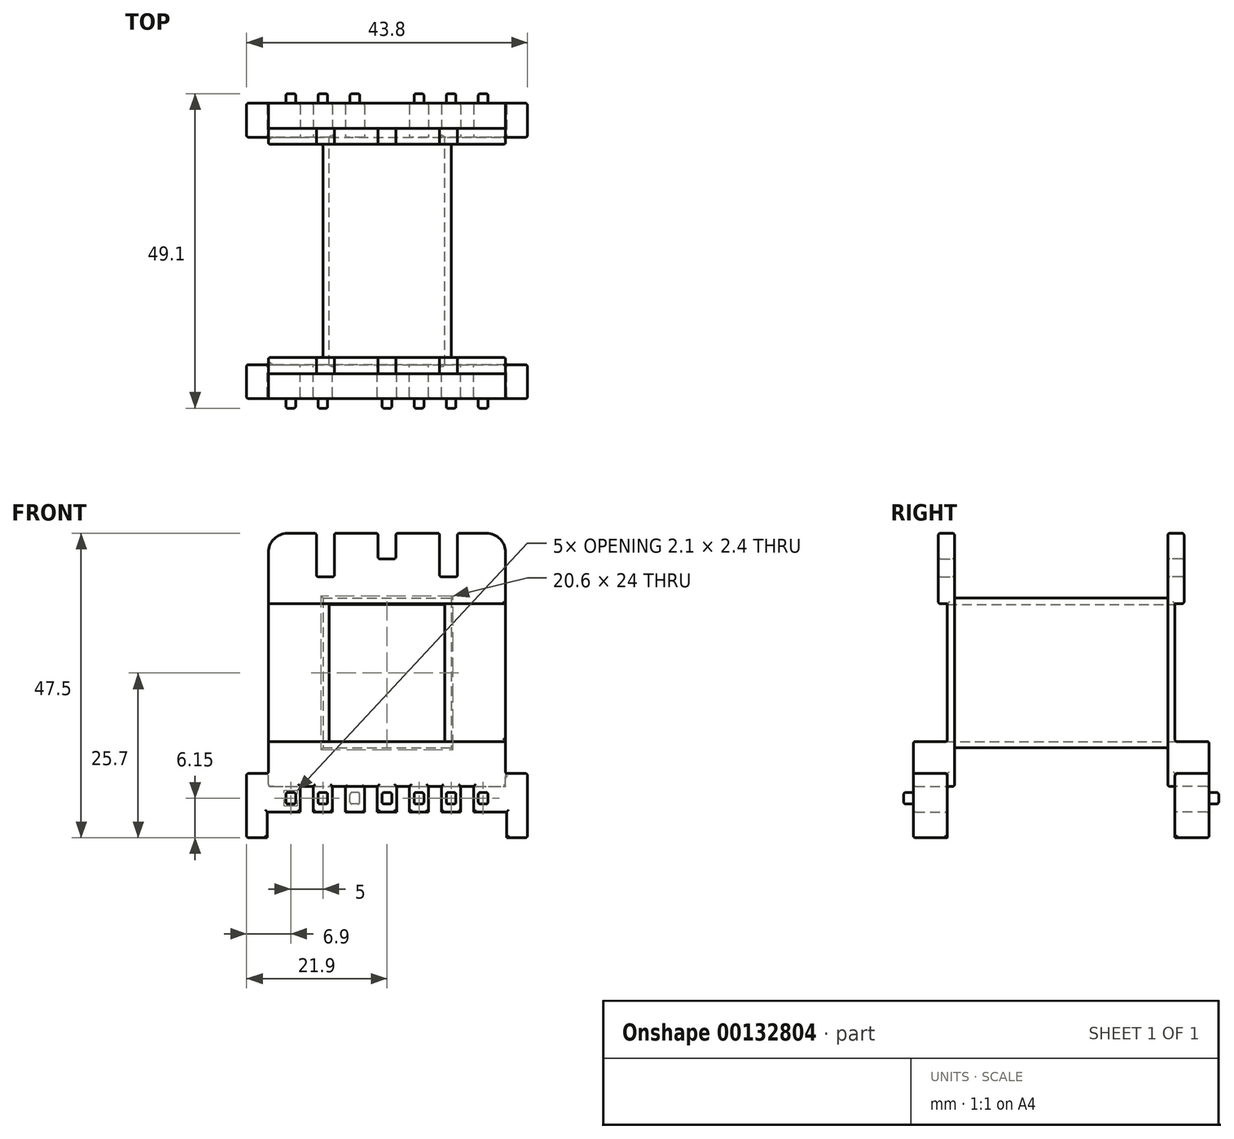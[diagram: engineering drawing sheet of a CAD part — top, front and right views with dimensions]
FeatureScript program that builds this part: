
annotation { "Feature Type Name" : "Feature", "Feature Type Description" : "" }
export const myFeature = defineFeature(function(context is Context, id is Id, definition is map)
    precondition{}
    {
        {
            var Q0;
            Q0=qCreatedBy(makeId("Front.planeOp"),FACE);
            var sketch = newSketch(context, id + "F0", { "sketchPlane" : qUnion([Q0])});
            skLineSegment(sketch, "E0.bottom", {"start": v(-18.5, 8) * mm, "end": v(18.5, 8) * mm});
            skLineSegment(sketch, "E0.left", {"start": v(-18.5, 8) * mm, "end": v(-18.5, 47.5) * mm});
            skLineSegment(sketch, "E0.right", {"start": v(18.5, 8) * mm, "end": v(18.5, 47.5) * mm});
            skLineSegment(sketch, "E1", {"start": v(-18.5, 47.5) * mm, "end": v(-11, 47.5) * mm});
            skLineSegment(sketch, "E2", {"start": v(-11, 47.5) * mm, "end": v(-11, 40.7) * mm});
            skLineSegment(sketch, "E3", {"start": v(-11, 40.7) * mm, "end": v(-8.2, 40.7) * mm});
            skLineSegment(sketch, "E4", {"start": v(-8.2, 40.7) * mm, "end": v(-8.2, 47.5) * mm});
            skLineSegment(sketch, "E5", {"start": v(-8.2, 47.5) * mm, "end": v(-1.4, 47.5) * mm});
            skLineSegment(sketch, "E6", {"start": v(-1.4, 47.5) * mm, "end": v(-1.4, 43.5) * mm});
            skLineSegment(sketch, "E7", {"start": v(-1.4, 43.5) * mm, "end": v(1.4, 43.5) * mm});
            skLineSegment(sketch, "E8", {"start": v(1.4, 43.5) * mm, "end": v(1.4, 47.5) * mm});
            skLineSegment(sketch, "E9", {"start": v(1.4, 47.5) * mm, "end": v(8.2, 47.5) * mm});
            skLineSegment(sketch, "E10", {"start": v(8.2, 47.5) * mm, "end": v(8.2, 40.7) * mm});
            skLineSegment(sketch, "E11", {"start": v(8.2, 40.7) * mm, "end": v(11, 40.7) * mm});
            skLineSegment(sketch, "E12", {"start": v(11, 40.7) * mm, "end": v(11, 47.5) * mm});
            skLineSegment(sketch, "E13", {"start": v(11, 47.5) * mm, "end": v(18.5, 47.5) * mm});
            skSolve(sketch);
        }
        {
            var Q0;
            Q0=makeQuery(id+"F0.imprint","IMPRINT",FACE,{"disambiguationData":[TD([[makeQuery(id+"F0.imprint","IMPRINT",EDGE,{"derivedFrom":sQuery(id+"F0.wireOp",EDGE,"E0.bottom")}),1.0]])]});
            var sketch = newSketch(context, id + "F1", { "sketchPlane" : qUnion([Q0])});
            skLineSegment(sketch, "E14.bottom", {"start": v(-9, 15) * mm, "end": v(9, 15) * mm});
            skLineSegment(sketch, "E14.top", {"start": v(-9, 36.4) * mm, "end": v(9, 36.4) * mm});
            skLineSegment(sketch, "E14.left", {"start": v(-9, 15) * mm, "end": v(-9, 36.4) * mm});
            skLineSegment(sketch, "E14.right", {"start": v(9, 15) * mm, "end": v(9, 36.4) * mm});
            skSolve(sketch);
        }
        {
            var Q0;
            Q0=makeQuery(id+"F1.imprint","IMPRINT",FACE,{"disambiguationData":[TD([[makeQuery(id+"F1.imprint","IMPRINT",EDGE,{"derivedFrom":sQuery(id+"F1.wireOp",EDGE,"E14.bottom")}),-1.0]])]});
            extrude(context, id + "F2", {"entities" : qUnion([Q0]), "depth" : 17.75 * mm, "hasSecondDirection" : true, "secondDirectionOppositeDirection" : false, "secondDirectionDepth" : 16.65 * mm});
        }
        {
            var Q0;
            Q0=makeQuery(id+"F2.opExtrude","SWEPT_BODY",BODY,{"disambiguationData":[OSD([sQuery(id+"F0.wireOp",EDGE,"E0.bottom"),sQuery(id+"F0.wireOp",EDGE,"E0.top"),sQuery(id+"F0.wireOp",EDGE,"E0.left"),sQuery(id+"F0.wireOp",EDGE,"E0.right"),sQuery(id+"F1.wireOp",EDGE,"E14.bottom"),sQuery(id+"F1.wireOp",EDGE,"E14.top"),sQuery(id+"F1.wireOp",EDGE,"E14.left"),sQuery(id+"F1.wireOp",EDGE,"E14.right")])]});
            var Q1;
            Q1=makeQuery(id+"F0.imprint","IMPRINT",FACE,{"disambiguationData":[TD([[makeQuery(id+"F0.imprint","IMPRINT",EDGE,{"derivedFrom":sQuery(id+"F0.wireOp",EDGE,"E0.bottom")}),1.0]])]});
            mirror(context, id + "F3", {"operationType" : NewBodyOperationType.ADD, "entities" : qUnion([Q0]), "mirrorPlane" : qUnion([Q1])});
        }
        {
            var Q0;
            Q0=makeQuery(id+"F0.imprint","IMPRINT",FACE,{"disambiguationData":[TD([[makeQuery(id+"F0.imprint","IMPRINT",EDGE,{"derivedFrom":sQuery(id+"F0.wireOp",EDGE,"E0.bottom")}),1.0]])]});
            var sketch = newSketch(context, id + "F4", { "sketchPlane" : qUnion([Q0])});
            skLineSegment(sketch, "E15.bottom", {"start": v(-10, 37.4) * mm, "end": v(10, 37.4) * mm});
            skLineSegment(sketch, "E15.top", {"start": v(-10, 14) * mm, "end": v(10, 14) * mm});
            skLineSegment(sketch, "E15.left", {"start": v(-10, 37.4) * mm, "end": v(-10, 14) * mm});
            skLineSegment(sketch, "E15.right", {"start": v(10, 37.4) * mm, "end": v(10, 14) * mm});
            skSolve(sketch);
        }
        {
            var Q0;
            Q0=makeQuery(id+"F4.imprint","IMPRINT",FACE,{"disambiguationData":[TD([[makeQuery(id+"F4.imprint","IMPRINT",EDGE,{"derivedFrom":sQuery(id+"F4.wireOp",EDGE,"E15.bottom")}),-1.0]])]});
            var sketch = newSketch(context, id + "F5", { "sketchPlane" : qUnion([Q0])});
            skLineSegment(sketch, "E16.bottom", {"start": v(-9, 36.4) * mm, "end": v(9, 36.4) * mm});
            skLineSegment(sketch, "E16.top", {"start": v(-9, 15) * mm, "end": v(9, 15) * mm});
            skLineSegment(sketch, "E16.left", {"start": v(-9, 36.4) * mm, "end": v(-9, 15) * mm});
            skLineSegment(sketch, "E16.right", {"start": v(9, 36.4) * mm, "end": v(9, 15) * mm});
            skSolve(sketch);
        }
        {
            var Q0;
            Q0=makeQuery(id+"F5.imprint","IMPRINT",FACE,{"disambiguationData":[TD([[makeQuery(id+"F5.imprint","IMPRINT",EDGE,{"derivedFrom":sQuery(id+"F5.wireOp",EDGE,"E16.bottom")}),1.0]])]});
            extrude(context, id + "F6", {"entities" : qUnion([Q0]), "operationType" : NewBodyOperationType.ADD, "endBound" : BoundingType.SYMMETRIC, "depth" : 35 * mm});
        }
        {
            var Q0;
            Q0=makeQuery(id+"F2.opExtrude","CAP_FACE",FACE,{"disambiguationData":[OSD([sQuery(id+"F0.wireOp",EDGE,"E0.bottom"),sQuery(id+"F0.wireOp",EDGE,"E0.top"),sQuery(id+"F0.wireOp",EDGE,"E0.left"),sQuery(id+"F0.wireOp",EDGE,"E0.right"),sQuery(id+"F1.wireOp",EDGE,"E14.bottom"),sQuery(id+"F1.wireOp",EDGE,"E14.top"),sQuery(id+"F1.wireOp",EDGE,"E14.left"),sQuery(id+"F1.wireOp",EDGE,"E14.right")])],"isStart":false});
            var sketch = newSketch(context, id + "F7", { "sketchPlane" : qUnion([Q0])});
            skLineSegment(sketch, "E17", {"start": v(-21.9, 0) * mm, "end": v(-21.9, 10) * mm});
            skLineSegment(sketch, "E18", {"start": v(-21.9, 10) * mm, "end": v(-18.5, 10) * mm});
            skLineSegment(sketch, "E19", {"start": v(-18.5, 10) * mm, "end": v(-18.5, 15) * mm});
            skLineSegment(sketch, "E20", {"start": v(-18.5, 15) * mm, "end": v(18.5, 15) * mm});
            skLineSegment(sketch, "E21", {"start": v(18.5, 15) * mm, "end": v(18.5, 10) * mm});
            skLineSegment(sketch, "E22", {"start": v(18.5, 10) * mm, "end": v(21.9, 10) * mm});
            skLineSegment(sketch, "E23", {"start": v(21.9, 10) * mm, "end": v(21.9, 0) * mm});
            skLineSegment(sketch, "E24", {"start": v(21.9, 0) * mm, "end": v(18.65, 0) * mm});
            skLineSegment(sketch, "E25", {"start": v(18.65, 0) * mm, "end": v(18.65, 4) * mm});
            skLineSegment(sketch, "E26", {"start": v(-18.65, 4) * mm, "end": v(-18.65, 0) * mm});
            skLineSegment(sketch, "E27", {"start": v(-18.65, 0) * mm, "end": v(-21.9, 0) * mm});
            skLineSegment(sketch, "E28", {"start": v(-18.65, 4) * mm, "end": v(-13.5, 4) * mm});
            skLineSegment(sketch, "E29", {"start": v(-13.5, 4) * mm, "end": v(-13.5, 8) * mm});
            skLineSegment(sketch, "E30", {"start": v(-13.5, 8) * mm, "end": v(-11.5, 8) * mm});
            skLineSegment(sketch, "E31", {"start": v(-11.5, 8) * mm, "end": v(-11.5, 4) * mm});
            skLineSegment(sketch, "E32", {"start": v(-11.5, 4) * mm, "end": v(-8.5, 4) * mm});
            skLineSegment(sketch, "E33", {"start": v(-8.5, 4) * mm, "end": v(-8.5, 8) * mm});
            skLineSegment(sketch, "E34", {"start": v(-8.5, 8) * mm, "end": v(-1.5, 8) * mm});
            skLineSegment(sketch, "E35", {"start": v(-1.5, 8) * mm, "end": v(-1.5, 4) * mm});
            skLineSegment(sketch, "E36", {"start": v(-1.5, 4) * mm, "end": v(0, 4) * mm});
            skLineSegment(sketch, "E37.MirrorCS", {"start": v(13.5, 8) * mm, "end": v(11.5, 8) * mm});
            skLineSegment(sketch, "E38.MirrorCS", {"start": v(6.5, 4) * mm, "end": v(3.5, 4) * mm});
            skLineSegment(sketch, "E39.MirrorCS", {"start": v(8.5, 8) * mm, "end": v(6.5, 8) * mm});
            skLineSegment(sketch, "E40.MirrorCS", {"start": v(11.5, 8) * mm, "end": v(11.5, 4) * mm});
            skLineSegment(sketch, "E41.MirrorCS", {"start": v(6.5, 8) * mm, "end": v(6.5, 4) * mm});
            skLineSegment(sketch, "E42.MirrorCS", {"start": v(1.5, 8) * mm, "end": v(1.5, 4) * mm});
            skLineSegment(sketch, "E43.MirrorCS", {"start": v(1.5, 4) * mm, "end": v(0, 4) * mm});
            skLineSegment(sketch, "E44.MirrorCS", {"start": v(13.5, 4) * mm, "end": v(13.5, 8) * mm});
            skLineSegment(sketch, "E45.MirrorCS", {"start": v(3.5, 4) * mm, "end": v(3.5, 8) * mm});
            skLineSegment(sketch, "E46.MirrorCS", {"start": v(11.5, 4) * mm, "end": v(8.5, 4) * mm});
            skLineSegment(sketch, "E47.MirrorCS", {"start": v(18.65, 4) * mm, "end": v(13.5, 4) * mm});
            skLineSegment(sketch, "E48.MirrorCS", {"start": v(18.65, 4) * mm, "end": v(18.65, 0) * mm});
            skLineSegment(sketch, "E49.MirrorCS", {"start": v(3.5, 8) * mm, "end": v(1.5, 8) * mm});
            skLineSegment(sketch, "E50.MirrorCS", {"start": v(8.5, 4) * mm, "end": v(8.5, 8) * mm});
            skSolve(sketch);
        }
        {
            var Q0;
            {var subQ8=sQuery(id+"F7.wireOp",EDGE,"E19");Q0=makeQuery(id+"F7.imprint","IMPRINT",FACE,{"disambiguationData":[TD([[makeQuery(id+"F7.imprint","IMPRINT",EDGE,{"derivedFrom":subQ8}),-1.0]])]});}
            var Q1;
            Q1=makeQuery(id+"F7.imprint","IMPRINT",FACE,{"disambiguationData":[TD([[makeQuery(id+"F7.imprint","IMPRINT",EDGE,{"derivedFrom":sQuery(id+"F7.wireOp",EDGE,"E17")}),-1.0]])]});
            var Q2;
            {var subQ3=sQuery(id+"F7.wireOp",EDGE,"E31");Q2=makeQuery(id+"F7.imprint","IMPRINT",FACE,{"disambiguationData":[TD([[makeQuery(id+"F7.imprint","IMPRINT",EDGE,{"derivedFrom":subQ3}),1.0]])]});}
            var Q3;
            {var subQ3=sQuery(id+"F7.wireOp",EDGE,"73ZmB12o-aMWT-i6gB-7MlO-vDFuIAe7J9VM");Q3=makeQuery(id+"F7.imprint","IMPRINT",FACE,{"disambiguationData":[TD([[makeQuery(id+"F7.imprint","IMPRINT",EDGE,{"derivedFrom":subQ3}),1.0]])]});}
            var Q4;
            {var subQ1=sQuery(id+"F7.wireOp",EDGE,"E35");Q4=makeQuery(id+"F7.imprint","IMPRINT",FACE,{"disambiguationData":[TD([[makeQuery(id+"F7.imprint","IMPRINT",EDGE,{"derivedFrom":subQ1}),1.0]])]});}
            var Q5;
            {var subQ1=sQuery(id+"F7.wireOp",EDGE,"E41.MirrorCS");Q5=makeQuery(id+"F7.imprint","IMPRINT",FACE,{"disambiguationData":[TD([[makeQuery(id+"F7.imprint","IMPRINT",EDGE,{"derivedFrom":subQ1}),-1.0]])]});}
            var Q6;
            {var subQ3=sQuery(id+"F7.wireOp",EDGE,"E40.MirrorCS");Q6=makeQuery(id+"F7.imprint","IMPRINT",FACE,{"disambiguationData":[TD([[makeQuery(id+"F7.imprint","IMPRINT",EDGE,{"derivedFrom":subQ3}),-1.0]])]});}
            var Q7;
            {var subQ1=sQuery(id+"F7.wireOp",EDGE,"E22");Q7=makeQuery(id+"F7.imprint","IMPRINT",FACE,{"disambiguationData":[TD([[makeQuery(id+"F7.imprint","IMPRINT",EDGE,{"derivedFrom":subQ1}),-1.0]])]});}
            extrude(context, id + "F8", {"entities" : qUnion([Q0, Q1, Q2, Q3, Q4, Q5, Q6, Q7]), "operationType" : NewBodyOperationType.ADD, "depth" : 5.3 * mm});
        }
        {
            var Q0;
            Q0=makeQuery(id+"F3.opPattern","COPY",FACE,{"derivedFrom":makeQuery(id+"F2.opExtrude","CAP_FACE",FACE,{"disambiguationData":[OSD([sQuery(id+"F0.wireOp",EDGE,"E0.bottom"),sQuery(id+"F0.wireOp",EDGE,"E0.top"),sQuery(id+"F0.wireOp",EDGE,"E0.left"),sQuery(id+"F0.wireOp",EDGE,"E0.right"),sQuery(id+"F1.wireOp",EDGE,"E14.bottom"),sQuery(id+"F1.wireOp",EDGE,"E14.top"),sQuery(id+"F1.wireOp",EDGE,"E14.left"),sQuery(id+"F1.wireOp",EDGE,"E14.right")])],"isStart":false}),"instanceName":"1"});
            var sketch = newSketch(context, id + "F9", { "sketchPlane" : qUnion([Q0])});
            skLineSegment(sketch, "E51", {"start": v(-21.9, 0) * mm, "end": v(-21.9, 10) * mm});
            skLineSegment(sketch, "E52", {"start": v(-21.9, 10) * mm, "end": v(-18.5, 10) * mm});
            skLineSegment(sketch, "E53", {"start": v(-18.5, 10) * mm, "end": v(-18.5, 15) * mm});
            skLineSegment(sketch, "E54", {"start": v(-18.5, 15) * mm, "end": v(18.5, 15) * mm});
            skLineSegment(sketch, "E55", {"start": v(18.5, 15) * mm, "end": v(18.5, 10) * mm});
            skLineSegment(sketch, "E56", {"start": v(18.5, 10) * mm, "end": v(21.9, 10) * mm});
            skLineSegment(sketch, "E57", {"start": v(21.9, 10) * mm, "end": v(21.9, 0) * mm});
            skLineSegment(sketch, "E58", {"start": v(21.9, 0) * mm, "end": v(18.65, 0) * mm});
            skLineSegment(sketch, "E59", {"start": v(18.65, 0) * mm, "end": v(18.65, 4) * mm});
            skLineSegment(sketch, "E60", {"start": v(-18.65, 4) * mm, "end": v(-18.65, 0) * mm});
            skLineSegment(sketch, "E61", {"start": v(-18.65, 0) * mm, "end": v(-21.9, 0) * mm});
            skLineSegment(sketch, "E62", {"start": v(-18.65, 4) * mm, "end": v(-13.5, 4) * mm});
            skLineSegment(sketch, "E63", {"start": v(-13.5, 4) * mm, "end": v(-13.5, 8) * mm});
            skLineSegment(sketch, "E64", {"start": v(-13.5, 8) * mm, "end": v(-11.5, 8) * mm});
            skLineSegment(sketch, "E65", {"start": v(-11.5, 8) * mm, "end": v(-11.5, 4) * mm});
            skLineSegment(sketch, "E66", {"start": v(-11.5, 4) * mm, "end": v(-8.5, 4) * mm});
            skLineSegment(sketch, "E67", {"start": v(-8.5, 4) * mm, "end": v(-8.5, 8) * mm});
            skLineSegment(sketch, "E68", {"start": v(-8.5, 8) * mm, "end": v(-6.5, 8) * mm});
            skLineSegment(sketch, "E69", {"start": v(-6.5, 8) * mm, "end": v(-6.5, 4) * mm});
            skLineSegment(sketch, "E70", {"start": v(-6.5, 4) * mm, "end": v(-3.5, 4) * mm});
            skLineSegment(sketch, "E71", {"start": v(-3.5, 4) * mm, "end": v(-3.5, 8) * mm});
            skLineSegment(sketch, "E72", {"start": v(-3.5, 8) * mm, "end": v(3.5, 8) * mm});
            skLineSegment(sketch, "E73.MirrorCS", {"start": v(13.5, 8) * mm, "end": v(11.5, 8) * mm});
            skLineSegment(sketch, "E74.MirrorCS", {"start": v(8.5, 8) * mm, "end": v(6.5, 8) * mm});
            skLineSegment(sketch, "E75.MirrorCS", {"start": v(11.5, 8) * mm, "end": v(11.5, 4) * mm});
            skLineSegment(sketch, "E76.MirrorCS", {"start": v(6.5, 8) * mm, "end": v(6.5, 4) * mm});
            skLineSegment(sketch, "E77.MirrorCS", {"start": v(13.5, 4) * mm, "end": v(13.5, 8) * mm});
            skLineSegment(sketch, "E78.MirrorCS", {"start": v(3.5, 4) * mm, "end": v(3.5, 8) * mm});
            skLineSegment(sketch, "E79.MirrorCS", {"start": v(18.65, 4) * mm, "end": v(13.5, 4) * mm});
            skLineSegment(sketch, "E80.MirrorCS", {"start": v(8.5, 4) * mm, "end": v(8.5, 8) * mm});
            skLineSegment(sketch, "E81", {"start": v(3.5, 4) * mm, "end": v(6.5, 4) * mm});
            skLineSegment(sketch, "E82", {"start": v(8.5, 4) * mm, "end": v(11.5, 4) * mm});
            skSolve(sketch);
        }
        {
            var Q0;
            Q0=qSketchRegion(id+"F9",true);
            var Q1;
            Q1=qConstructionFilter(qBodyType(qCreatedBy(id+"F9",EDGE),BodyType.WIRE),ConstructionObject.NO);
            extrude(context, id + "F10", {"entities" : qUnion([Q0]), "operationType" : NewBodyOperationType.ADD, "surfaceEntities" : qUnion([Q1]), "depth" : 5.3 * mm});
        }
        {
            var Q0;
            Q0=makeQuery(id+"F2.opExtrude","CAP_FACE",FACE,{"disambiguationData":[OSD([sQuery(id+"F0.wireOp",EDGE,"E0.bottom"),sQuery(id+"F0.wireOp",EDGE,"E0.left"),sQuery(id+"F0.wireOp",EDGE,"E0.right"),sQuery(id+"F0.wireOp",EDGE,"E1"),sQuery(id+"F0.wireOp",EDGE,"E2"),sQuery(id+"F0.wireOp",EDGE,"E3"),sQuery(id+"F0.wireOp",EDGE,"E4"),sQuery(id+"F0.wireOp",EDGE,"E5"),sQuery(id+"F0.wireOp",EDGE,"E6"),sQuery(id+"F0.wireOp",EDGE,"E7"),sQuery(id+"F0.wireOp",EDGE,"E8"),sQuery(id+"F0.wireOp",EDGE,"E9"),sQuery(id+"F0.wireOp",EDGE,"E10"),sQuery(id+"F0.wireOp",EDGE,"E11"),sQuery(id+"F0.wireOp",EDGE,"E12"),sQuery(id+"F0.wireOp",EDGE,"E13"),sQuery(id+"F1.wireOp",EDGE,"E14.bottom"),sQuery(id+"F1.wireOp",EDGE,"E14.top"),sQuery(id+"F1.wireOp",EDGE,"E14.left"),sQuery(id+"F1.wireOp",EDGE,"E14.right")])],"isStart":false});
            var sketch = newSketch(context, id + "F11", { "sketchPlane" : qUnion([Q0])});
            skLineSegment(sketch, "E83", {"start": v(-18.5, 47.5) * mm, "end": v(-11, 47.5) * mm});
            skLineSegment(sketch, "E84", {"start": v(-11, 47.5) * mm, "end": v(-11, 40.7) * mm});
            skLineSegment(sketch, "E85", {"start": v(-11, 40.7) * mm, "end": v(-8.2, 40.7) * mm});
            skLineSegment(sketch, "E86", {"start": v(-8.2, 40.7) * mm, "end": v(-8.2, 47.5) * mm});
            skLineSegment(sketch, "E87", {"start": v(-8.2, 47.5) * mm, "end": v(-1.4, 47.5) * mm});
            skLineSegment(sketch, "E88", {"start": v(-1.4, 47.5) * mm, "end": v(-1.4, 43.5) * mm});
            skLineSegment(sketch, "E89", {"start": v(1.4, 43.5) * mm, "end": v(1.4, 47.5) * mm});
            skLineSegment(sketch, "E90", {"start": v(1.4, 47.5) * mm, "end": v(8.2, 47.5) * mm});
            skLineSegment(sketch, "E91", {"start": v(8.2, 47.5) * mm, "end": v(8.2, 40.7) * mm});
            skLineSegment(sketch, "E92", {"start": v(8.2, 40.7) * mm, "end": v(11, 40.7) * mm});
            skLineSegment(sketch, "E93", {"start": v(11, 40.7) * mm, "end": v(11, 47.5) * mm});
            skLineSegment(sketch, "E94", {"start": v(11, 47.5) * mm, "end": v(18.5, 47.5) * mm});
            skLineSegment(sketch, "E95", {"start": v(18.5, 47.5) * mm, "end": v(18.5, 36.5) * mm});
            skLineSegment(sketch, "E96", {"start": v(18.5, 36.5) * mm, "end": v(-18.5, 36.5) * mm});
            skLineSegment(sketch, "E97", {"start": v(-18.5, 36.5) * mm, "end": v(-18.5, 47.5) * mm});
            skSolve(sketch);
        }
        {
            var Q0;
            Q0=makeQuery(id+"F11.imprint","IMPRINT",FACE,{"disambiguationData":[TD([[makeQuery(id+"F11.imprint","IMPRINT",EDGE,{"derivedFrom":sQuery(id+"F11.wireOp",EDGE,"E83")}),-1.0]])]});
            extrude(context, id + "F12", {"entities" : qUnion([Q0]), "operationType" : NewBodyOperationType.ADD, "depth" : 1.4 * mm});
        }
        {
            var Q0;
            Q0=makeQuery(id+"F3.opPattern","COPY",FACE,{"derivedFrom":makeQuery(id+"F2.opExtrude","CAP_FACE",FACE,{"disambiguationData":[OSD([sQuery(id+"F0.wireOp",EDGE,"E0.bottom"),sQuery(id+"F0.wireOp",EDGE,"E0.left"),sQuery(id+"F0.wireOp",EDGE,"E0.right"),sQuery(id+"F0.wireOp",EDGE,"E1"),sQuery(id+"F0.wireOp",EDGE,"E2"),sQuery(id+"F0.wireOp",EDGE,"E3"),sQuery(id+"F0.wireOp",EDGE,"E4"),sQuery(id+"F0.wireOp",EDGE,"E5"),sQuery(id+"F0.wireOp",EDGE,"E6"),sQuery(id+"F0.wireOp",EDGE,"E7"),sQuery(id+"F0.wireOp",EDGE,"E8"),sQuery(id+"F0.wireOp",EDGE,"E9"),sQuery(id+"F0.wireOp",EDGE,"E10"),sQuery(id+"F0.wireOp",EDGE,"E11"),sQuery(id+"F0.wireOp",EDGE,"E12"),sQuery(id+"F0.wireOp",EDGE,"E13"),sQuery(id+"F1.wireOp",EDGE,"E14.bottom"),sQuery(id+"F1.wireOp",EDGE,"E14.top"),sQuery(id+"F1.wireOp",EDGE,"E14.left"),sQuery(id+"F1.wireOp",EDGE,"E14.right")])],"isStart":false}),"instanceName":"1"});
            var sketch = newSketch(context, id + "F13", { "sketchPlane" : qUnion([Q0])});
            skLineSegment(sketch, "E98", {"start": v(-18.5, 47.5) * mm, "end": v(-11, 47.5) * mm});
            skLineSegment(sketch, "E99", {"start": v(-11, 47.5) * mm, "end": v(-11, 40.7) * mm});
            skLineSegment(sketch, "E100", {"start": v(-11, 40.7) * mm, "end": v(-8.2, 40.7) * mm});
            skLineSegment(sketch, "E101", {"start": v(-8.2, 40.7) * mm, "end": v(-8.2, 47.5) * mm});
            skLineSegment(sketch, "E102", {"start": v(-8.2, 47.5) * mm, "end": v(-1.4, 47.5) * mm});
            skLineSegment(sketch, "E103", {"start": v(-1.4, 47.5) * mm, "end": v(-1.4, 43.5) * mm});
            skLineSegment(sketch, "E104", {"start": v(1.4, 43.5) * mm, "end": v(1.4, 47.5) * mm});
            skLineSegment(sketch, "E105", {"start": v(1.4, 47.5) * mm, "end": v(8.2, 47.5) * mm});
            skLineSegment(sketch, "E106", {"start": v(8.2, 47.5) * mm, "end": v(8.2, 40.7) * mm});
            skLineSegment(sketch, "E107", {"start": v(8.2, 40.7) * mm, "end": v(11, 40.7) * mm});
            skLineSegment(sketch, "E108", {"start": v(11, 40.7) * mm, "end": v(11, 47.5) * mm});
            skLineSegment(sketch, "E109", {"start": v(11, 47.5) * mm, "end": v(18.5, 47.5) * mm});
            skLineSegment(sketch, "E110", {"start": v(18.5, 47.5) * mm, "end": v(18.5, 36.5) * mm});
            skLineSegment(sketch, "E111", {"start": v(18.5, 36.5) * mm, "end": v(-18.5, 36.5) * mm});
            skLineSegment(sketch, "E112", {"start": v(-18.5, 36.5) * mm, "end": v(-18.5, 47.5) * mm});
            skLineSegment(sketch, "E113", {"start": v(-1.4, 43.5) * mm, "end": v(1.4, 43.5) * mm});
            skSolve(sketch);
        }
        {
            var Q0;
            Q0=makeQuery(id+"F13.imprint","IMPRINT",FACE,{"disambiguationData":[TD([[makeQuery(id+"F13.imprint","IMPRINT",EDGE,{"derivedFrom":sQuery(id+"F13.wireOp",EDGE,"E98")}),1.0]])]});
            extrude(context, id + "F14", {"entities" : qUnion([Q0]), "operationType" : NewBodyOperationType.ADD, "depth" : 1.4 * mm});
        }
        {
            var Q0;
            Q0=makeQuery(id+"F12.boolean.opBoolean","MERGE",EDGE,{"derivedFrom":[makeQuery(id+"F2.opExtrude","SWEPT_EDGE",EDGE,{"disambiguationData":[OSD([sQuery(id+"F0.wireOp",EDGE,"E0.right"),sQuery(id+"F0.wireOp",EDGE,"E13")])]}),makeQuery(id+"F12.opExtrude","SWEPT_EDGE",EDGE,{"disambiguationData":[OSD([sQuery(id+"F11.wireOp",EDGE,"E94"),sQuery(id+"F11.wireOp",EDGE,"E95")])]})]});
            var Q1;
            Q1=makeQuery(id+"F14.boolean.opBoolean","MERGE",EDGE,{"derivedFrom":[makeQuery(id+"F3.opPattern","COPY",EDGE,{"derivedFrom":makeQuery(id+"F2.opExtrude","SWEPT_EDGE",EDGE,{"disambiguationData":[OSD([sQuery(id+"F0.wireOp",EDGE,"E0.right"),sQuery(id+"F0.wireOp",EDGE,"E13")])]}),"instanceName":"1"}),makeQuery(id+"F14.opExtrude","SWEPT_EDGE",EDGE,{"disambiguationData":[OSD([sQuery(id+"F13.wireOp",EDGE,"E98"),sQuery(id+"F13.wireOp",EDGE,"E112")])]})]});
            var Q2;
            Q2=makeQuery(id+"F12.boolean.opBoolean","MERGE",EDGE,{"derivedFrom":[makeQuery(id+"F2.opExtrude","SWEPT_EDGE",EDGE,{"disambiguationData":[OSD([sQuery(id+"F0.wireOp",EDGE,"E0.left"),sQuery(id+"F0.wireOp",EDGE,"E1")])]}),makeQuery(id+"F12.opExtrude","SWEPT_EDGE",EDGE,{"disambiguationData":[OSD([sQuery(id+"F11.wireOp",EDGE,"E83"),sQuery(id+"F11.wireOp",EDGE,"E97")])]})]});
            var Q3;
            Q3=makeQuery(id+"F14.boolean.opBoolean","MERGE",EDGE,{"derivedFrom":[makeQuery(id+"F3.opPattern","COPY",EDGE,{"derivedFrom":makeQuery(id+"F2.opExtrude","SWEPT_EDGE",EDGE,{"disambiguationData":[OSD([sQuery(id+"F0.wireOp",EDGE,"E0.left"),sQuery(id+"F0.wireOp",EDGE,"E1")])]}),"instanceName":"1"}),makeQuery(id+"F14.opExtrude","SWEPT_EDGE",EDGE,{"disambiguationData":[OSD([sQuery(id+"F13.wireOp",EDGE,"E109"),sQuery(id+"F13.wireOp",EDGE,"E110")])]})]});
            fillet(context, id + "F15", {"entities" : qUnion([Q0, Q1, Q2, Q3]), "radius" : 3 * mm, "tangentPropagation" : true, "allowEdgeOverflow" : false});
        }
        {
            var Q0;
            Q0=makeQuery(id+"F10.opExtrude","CAP_FACE",FACE,{"disambiguationData":[OSD([sQuery(id+"F9.wireOp",EDGE,"E51"),sQuery(id+"F9.wireOp",EDGE,"E52"),sQuery(id+"F9.wireOp",EDGE,"E53"),sQuery(id+"F9.wireOp",EDGE,"E54"),sQuery(id+"F9.wireOp",EDGE,"E55"),sQuery(id+"F9.wireOp",EDGE,"E56"),sQuery(id+"F9.wireOp",EDGE,"E57"),sQuery(id+"F9.wireOp",EDGE,"E58"),sQuery(id+"F9.wireOp",EDGE,"E59"),sQuery(id+"F9.wireOp",EDGE,"E60"),sQuery(id+"F9.wireOp",EDGE,"E61"),sQuery(id+"F9.wireOp",EDGE,"E62"),sQuery(id+"F9.wireOp",EDGE,"E63"),sQuery(id+"F9.wireOp",EDGE,"E64"),sQuery(id+"F9.wireOp",EDGE,"E65"),sQuery(id+"F9.wireOp",EDGE,"E66"),sQuery(id+"F9.wireOp",EDGE,"E67"),sQuery(id+"F9.wireOp",EDGE,"E68"),sQuery(id+"F9.wireOp",EDGE,"E69"),sQuery(id+"F9.wireOp",EDGE,"E70"),sQuery(id+"F9.wireOp",EDGE,"E71"),sQuery(id+"F9.wireOp",EDGE,"E72"),sQuery(id+"F9.wireOp",EDGE,"E73.MirrorCS"),sQuery(id+"F9.wireOp",EDGE,"E74.MirrorCS"),sQuery(id+"F9.wireOp",EDGE,"E75.MirrorCS"),sQuery(id+"F9.wireOp",EDGE,"E76.MirrorCS"),sQuery(id+"F9.wireOp",EDGE,"E77.MirrorCS"),sQuery(id+"F9.wireOp",EDGE,"E78.MirrorCS"),sQuery(id+"F9.wireOp",EDGE,"E79.MirrorCS"),sQuery(id+"F9.wireOp",EDGE,"E80.MirrorCS"),sQuery(id+"F9.wireOp",EDGE,"E81"),sQuery(id+"F9.wireOp",EDGE,"E82")])],"isStart":false});
            var sketch = newSketch(context, id + "F16", { "sketchPlane" : qUnion([Q0])});
            skLineSegment(sketch, "E114.bottom", {"start": v(-15.75, 5.25) * mm, "end": v(-14.25, 5.25) * mm});
            skLineSegment(sketch, "E114.top", {"start": v(-15.75, 7.05) * mm, "end": v(-14.25, 7.05) * mm});
            skLineSegment(sketch, "E114.left", {"start": v(-15.75, 5.25) * mm, "end": v(-15.75, 7.05) * mm});
            skLineSegment(sketch, "E114.right", {"start": v(-14.25, 5.25) * mm, "end": v(-14.25, 7.05) * mm});
            skLineSegment(sketch, "E115.bottom", {"start": v(-10.75, 5.25) * mm, "end": v(-9.25, 5.25) * mm});
            skLineSegment(sketch, "E115.top", {"start": v(-10.75, 7.05) * mm, "end": v(-9.25, 7.05) * mm});
            skLineSegment(sketch, "E115.left", {"start": v(-10.75, 5.25) * mm, "end": v(-10.75, 7.05) * mm});
            skLineSegment(sketch, "E115.right", {"start": v(-9.25, 5.25) * mm, "end": v(-9.25, 7.05) * mm});
            skLineSegment(sketch, "E116.bottom", {"start": v(-5.75, 5.25) * mm, "end": v(-4.25, 5.25) * mm});
            skLineSegment(sketch, "E116.top", {"start": v(-5.75, 7.05) * mm, "end": v(-4.25, 7.05) * mm});
            skLineSegment(sketch, "E116.left", {"start": v(-5.75, 5.25) * mm, "end": v(-5.75, 7.05) * mm});
            skLineSegment(sketch, "E116.right", {"start": v(-4.25, 5.25) * mm, "end": v(-4.25, 7.05) * mm});
            skLineSegment(sketch, "E117.bottom", {"start": v(4.25, 5.25) * mm, "end": v(5.75, 5.25) * mm});
            skLineSegment(sketch, "E117.top", {"start": v(4.25, 7.05) * mm, "end": v(5.75, 7.05) * mm});
            skLineSegment(sketch, "E117.left", {"start": v(4.25, 5.25) * mm, "end": v(4.25, 7.05) * mm});
            skLineSegment(sketch, "E117.right", {"start": v(5.75, 5.25) * mm, "end": v(5.75, 7.05) * mm});
            skLineSegment(sketch, "E118.bottom", {"start": v(9.25, 5.25) * mm, "end": v(10.75, 5.25) * mm});
            skLineSegment(sketch, "E118.top", {"start": v(9.25, 7.05) * mm, "end": v(10.75, 7.05) * mm});
            skLineSegment(sketch, "E118.left", {"start": v(9.25, 5.25) * mm, "end": v(9.25, 7.05) * mm});
            skLineSegment(sketch, "E118.right", {"start": v(10.75, 5.25) * mm, "end": v(10.75, 7.05) * mm});
            skPoint(sketch, "E119.oppositeSnap0", {"position": v(10, 7.05) * mm});
            skLineSegment(sketch, "E119.bottom", {"start": v(14.25, 5.25) * mm, "end": v(15.75, 5.25) * mm});
            skLineSegment(sketch, "E119.top", {"start": v(14.25, 7.05) * mm, "end": v(15.75, 7.05) * mm});
            skLineSegment(sketch, "E119.left", {"start": v(14.25, 5.25) * mm, "end": v(14.25, 7.05) * mm});
            skLineSegment(sketch, "E119.right", {"start": v(15.75, 5.25) * mm, "end": v(15.75, 7.05) * mm});
            skSolve(sketch);
        }
        {
            var Q0;
            Q0=makeQuery(id+"F8.opExtrude","CAP_FACE",FACE,{"disambiguationData":[OSD([sQuery(id+"F7.wireOp",EDGE,"E17"),sQuery(id+"F7.wireOp",EDGE,"E18"),sQuery(id+"F7.wireOp",EDGE,"E19"),sQuery(id+"F7.wireOp",EDGE,"E20"),sQuery(id+"F7.wireOp",EDGE,"E21"),sQuery(id+"F7.wireOp",EDGE,"E22"),sQuery(id+"F7.wireOp",EDGE,"E23"),sQuery(id+"F7.wireOp",EDGE,"E24"),sQuery(id+"F7.wireOp",EDGE,"E26"),sQuery(id+"F7.wireOp",EDGE,"E27"),sQuery(id+"F7.wireOp",EDGE,"E28"),sQuery(id+"F7.wireOp",EDGE,"E29"),sQuery(id+"F7.wireOp",EDGE,"E30"),sQuery(id+"F7.wireOp",EDGE,"E31"),sQuery(id+"F7.wireOp",EDGE,"E32"),sQuery(id+"F7.wireOp",EDGE,"E33"),sQuery(id+"F7.wireOp",EDGE,"E34"),sQuery(id+"F7.wireOp",EDGE,"E35"),sQuery(id+"F7.wireOp",EDGE,"E36"),sQuery(id+"F7.wireOp",EDGE,"E37.MirrorCS"),sQuery(id+"F7.wireOp",EDGE,"E38.MirrorCS"),sQuery(id+"F7.wireOp",EDGE,"E39.MirrorCS"),sQuery(id+"F7.wireOp",EDGE,"E40.MirrorCS"),sQuery(id+"F7.wireOp",EDGE,"E41.MirrorCS"),sQuery(id+"F7.wireOp",EDGE,"E42.MirrorCS"),sQuery(id+"F7.wireOp",EDGE,"E43.MirrorCS"),sQuery(id+"F7.wireOp",EDGE,"E44.MirrorCS"),sQuery(id+"F7.wireOp",EDGE,"E45.MirrorCS"),sQuery(id+"F7.wireOp",EDGE,"E46.MirrorCS"),sQuery(id+"F7.wireOp",EDGE,"E47.MirrorCS"),sQuery(id+"F7.wireOp",EDGE,"E48.MirrorCS"),sQuery(id+"F7.wireOp",EDGE,"E49.MirrorCS"),sQuery(id+"F7.wireOp",EDGE,"E50.MirrorCS")])],"isStart":false});
            var sketch = newSketch(context, id + "F17", { "sketchPlane" : qUnion([Q0])});
            skLineSegment(sketch, "E120.bottom", {"start": v(-15.75, 5.25) * mm, "end": v(-14.25, 5.25) * mm});
            skLineSegment(sketch, "E120.top", {"start": v(-15.75, 7.05) * mm, "end": v(-14.25, 7.05) * mm});
            skLineSegment(sketch, "E120.left", {"start": v(-15.75, 5.25) * mm, "end": v(-15.75, 7.05) * mm});
            skLineSegment(sketch, "E120.right", {"start": v(-14.25, 5.25) * mm, "end": v(-14.25, 7.05) * mm});
            skLineSegment(sketch, "E121.bottom", {"start": v(-10.75, 5.25) * mm, "end": v(-9.25, 5.25) * mm});
            skLineSegment(sketch, "E121.top", {"start": v(-10.75, 7.05) * mm, "end": v(-9.25, 7.05) * mm});
            skLineSegment(sketch, "E121.left", {"start": v(-10.75, 5.25) * mm, "end": v(-10.75, 7.05) * mm});
            skLineSegment(sketch, "E121.right", {"start": v(-9.25, 5.25) * mm, "end": v(-9.25, 7.05) * mm});
            skLineSegment(sketch, "E122.bottom", {"start": v(-0.75, 5.25) * mm, "end": v(0.75, 5.25) * mm});
            skLineSegment(sketch, "E122.top", {"start": v(-0.75, 7.05) * mm, "end": v(0.75, 7.05) * mm});
            skLineSegment(sketch, "E122.left", {"start": v(-0.75, 5.25) * mm, "end": v(-0.75, 7.05) * mm});
            skLineSegment(sketch, "E122.right", {"start": v(0.75, 5.25) * mm, "end": v(0.75, 7.05) * mm});
            skLineSegment(sketch, "E123.bottom", {"start": v(4.25, 5.25) * mm, "end": v(5.75, 5.25) * mm});
            skLineSegment(sketch, "E123.top", {"start": v(4.25, 7.05) * mm, "end": v(5.75, 7.05) * mm});
            skLineSegment(sketch, "E123.left", {"start": v(4.25, 5.25) * mm, "end": v(4.25, 7.05) * mm});
            skLineSegment(sketch, "E123.right", {"start": v(5.75, 5.25) * mm, "end": v(5.75, 7.05) * mm});
            skLineSegment(sketch, "E124.bottom", {"start": v(9.25, 5.25) * mm, "end": v(10.75, 5.25) * mm});
            skLineSegment(sketch, "E124.top", {"start": v(9.25, 7.05) * mm, "end": v(10.75, 7.05) * mm});
            skLineSegment(sketch, "E124.left", {"start": v(9.25, 5.25) * mm, "end": v(9.25, 7.05) * mm});
            skLineSegment(sketch, "E124.right", {"start": v(10.75, 5.25) * mm, "end": v(10.75, 7.05) * mm});
            skPoint(sketch, "E125.oppositeSnap0", {"position": v(10, 7.05) * mm});
            skLineSegment(sketch, "E125.bottom", {"start": v(14.25, 5.25) * mm, "end": v(15.75, 5.25) * mm});
            skLineSegment(sketch, "E125.top", {"start": v(14.25, 7.05) * mm, "end": v(15.75, 7.05) * mm});
            skLineSegment(sketch, "E125.left", {"start": v(14.25, 5.25) * mm, "end": v(14.25, 7.05) * mm});
            skLineSegment(sketch, "E125.right", {"start": v(15.75, 5.25) * mm, "end": v(15.75, 7.05) * mm});
            skSolve(sketch);
        }
        {
            var Q0;
            Q0=makeQuery(id+"F16.imprint","IMPRINT",FACE,{"disambiguationData":[TD([[makeQuery(id+"F16.imprint","IMPRINT",EDGE,{"derivedFrom":sQuery(id+"F16.wireOp",EDGE,"E114.bottom")}),1.0]])]});
            var Q1;
            Q1=makeQuery(id+"F16.imprint","IMPRINT",FACE,{"disambiguationData":[TD([[makeQuery(id+"F16.imprint","IMPRINT",EDGE,{"derivedFrom":sQuery(id+"F16.wireOp",EDGE,"E115.bottom")}),1.0]])]});
            var Q2;
            Q2=makeQuery(id+"F16.imprint","IMPRINT",FACE,{"disambiguationData":[TD([[makeQuery(id+"F16.imprint","IMPRINT",EDGE,{"derivedFrom":sQuery(id+"F16.wireOp",EDGE,"E116.bottom")}),1.0]])]});
            var Q3;
            Q3=makeQuery(id+"F16.imprint","IMPRINT",FACE,{"disambiguationData":[TD([[makeQuery(id+"F16.imprint","IMPRINT",EDGE,{"derivedFrom":sQuery(id+"F16.wireOp",EDGE,"E117.bottom")}),1.0]])]});
            var Q4;
            Q4=makeQuery(id+"F16.imprint","IMPRINT",FACE,{"disambiguationData":[TD([[makeQuery(id+"F16.imprint","IMPRINT",EDGE,{"derivedFrom":sQuery(id+"F16.wireOp",EDGE,"E118.bottom")}),1.0]])]});
            var Q5;
            Q5=makeQuery(id+"F16.imprint","IMPRINT",FACE,{"disambiguationData":[TD([[makeQuery(id+"F16.imprint","IMPRINT",EDGE,{"derivedFrom":sQuery(id+"F16.wireOp",EDGE,"E119.bottom")}),1.0]])]});
            extrude(context, id + "F18", {"entities" : qUnion([Q0, Q1, Q2, Q3, Q4, Q5]), "operationType" : NewBodyOperationType.ADD, "depth" : 1.5 * mm});
        }
        {
            var Q0;
            Q0=makeQuery(id+"F17.imprint","IMPRINT",FACE,{"disambiguationData":[TD([[makeQuery(id+"F17.imprint","IMPRINT",EDGE,{"derivedFrom":sQuery(id+"F17.wireOp",EDGE,"E120.bottom")}),1.0]])]});
            var Q1;
            Q1=makeQuery(id+"F17.imprint","IMPRINT",FACE,{"disambiguationData":[TD([[makeQuery(id+"F17.imprint","IMPRINT",EDGE,{"derivedFrom":sQuery(id+"F17.wireOp",EDGE,"E121.bottom")}),1.0]])]});
            var Q2;
            Q2=makeQuery(id+"F17.imprint","IMPRINT",FACE,{"disambiguationData":[TD([[makeQuery(id+"F17.imprint","IMPRINT",EDGE,{"derivedFrom":sQuery(id+"F17.wireOp",EDGE,"E125.bottom")}),1.0]])]});
            var Q3;
            Q3=makeQuery(id+"F17.imprint","IMPRINT",FACE,{"disambiguationData":[TD([[makeQuery(id+"F17.imprint","IMPRINT",EDGE,{"derivedFrom":sQuery(id+"F17.wireOp",EDGE,"E124.bottom")}),1.0]])]});
            var Q4;
            Q4=makeQuery(id+"F17.imprint","IMPRINT",FACE,{"disambiguationData":[TD([[makeQuery(id+"F17.imprint","IMPRINT",EDGE,{"derivedFrom":sQuery(id+"F17.wireOp",EDGE,"E123.bottom")}),1.0]])]});
            var Q5;
            Q5=makeQuery(id+"F17.imprint","IMPRINT",FACE,{"disambiguationData":[TD([[makeQuery(id+"F17.imprint","IMPRINT",EDGE,{"derivedFrom":sQuery(id+"F17.wireOp",EDGE,"E122.bottom")}),1.0]])]});
            extrude(context, id + "F19", {"entities" : qUnion([Q0, Q1, Q2, Q3, Q4, Q5]), "operationType" : NewBodyOperationType.ADD, "depth" : 1.5 * mm});
        }
        {
            var Q0;
            Q0=makeQuery(id+"F2.opExtrude","CAP_FACE",FACE,{"disambiguationData":[OSD([sQuery(id+"F0.wireOp",EDGE,"E0.bottom"),sQuery(id+"F0.wireOp",EDGE,"E0.left"),sQuery(id+"F0.wireOp",EDGE,"E0.right"),sQuery(id+"F0.wireOp",EDGE,"E1"),sQuery(id+"F0.wireOp",EDGE,"E2"),sQuery(id+"F0.wireOp",EDGE,"E3"),sQuery(id+"F0.wireOp",EDGE,"E4"),sQuery(id+"F0.wireOp",EDGE,"E5"),sQuery(id+"F0.wireOp",EDGE,"E6"),sQuery(id+"F0.wireOp",EDGE,"E7"),sQuery(id+"F0.wireOp",EDGE,"E8"),sQuery(id+"F0.wireOp",EDGE,"E9"),sQuery(id+"F0.wireOp",EDGE,"E10"),sQuery(id+"F0.wireOp",EDGE,"E11"),sQuery(id+"F0.wireOp",EDGE,"E12"),sQuery(id+"F0.wireOp",EDGE,"E13"),sQuery(id+"F1.wireOp",EDGE,"E14.bottom"),sQuery(id+"F1.wireOp",EDGE,"E14.top"),sQuery(id+"F1.wireOp",EDGE,"E14.left"),sQuery(id+"F1.wireOp",EDGE,"E14.right")])],"isStart":true});
            var Q1;
            Q1=makeQuery(id+"F3.opPattern","COPY",FACE,{"derivedFrom":makeQuery(id+"F2.opExtrude","CAP_FACE",FACE,{"disambiguationData":[OSD([sQuery(id+"F0.wireOp",EDGE,"E0.bottom"),sQuery(id+"F0.wireOp",EDGE,"E0.left"),sQuery(id+"F0.wireOp",EDGE,"E0.right"),sQuery(id+"F0.wireOp",EDGE,"E1"),sQuery(id+"F0.wireOp",EDGE,"E2"),sQuery(id+"F0.wireOp",EDGE,"E3"),sQuery(id+"F0.wireOp",EDGE,"E4"),sQuery(id+"F0.wireOp",EDGE,"E5"),sQuery(id+"F0.wireOp",EDGE,"E6"),sQuery(id+"F0.wireOp",EDGE,"E7"),sQuery(id+"F0.wireOp",EDGE,"E8"),sQuery(id+"F0.wireOp",EDGE,"E9"),sQuery(id+"F0.wireOp",EDGE,"E10"),sQuery(id+"F0.wireOp",EDGE,"E11"),sQuery(id+"F0.wireOp",EDGE,"E12"),sQuery(id+"F0.wireOp",EDGE,"E13"),sQuery(id+"F1.wireOp",EDGE,"E14.bottom"),sQuery(id+"F1.wireOp",EDGE,"E14.top"),sQuery(id+"F1.wireOp",EDGE,"E14.left"),sQuery(id+"F1.wireOp",EDGE,"E14.right")])],"isStart":true}),"instanceName":"1"});
            var Q2;
            Q2=makeQuery(id+"F12.opExtrude","CAP_FACE",FACE,{"disambiguationData":[OSD([sQuery(id+"F0.wireOp",EDGE,"E7"),sQuery(id+"F11.wireOp",EDGE,"E83"),sQuery(id+"F11.wireOp",EDGE,"E84"),sQuery(id+"F11.wireOp",EDGE,"E85"),sQuery(id+"F11.wireOp",EDGE,"E86"),sQuery(id+"F11.wireOp",EDGE,"E87"),sQuery(id+"F11.wireOp",EDGE,"E88"),sQuery(id+"F11.wireOp",EDGE,"E89"),sQuery(id+"F11.wireOp",EDGE,"E90"),sQuery(id+"F11.wireOp",EDGE,"E91"),sQuery(id+"F11.wireOp",EDGE,"E92"),sQuery(id+"F11.wireOp",EDGE,"E93"),sQuery(id+"F11.wireOp",EDGE,"E94"),sQuery(id+"F11.wireOp",EDGE,"E95"),sQuery(id+"F11.wireOp",EDGE,"E96"),sQuery(id+"F11.wireOp",EDGE,"E97")])],"isStart":false});
            var Q3;
            Q3=makeQuery(id+"F8.opExtrude","CAP_FACE",FACE,{"disambiguationData":[OSD([sQuery(id+"F7.wireOp",EDGE,"E17"),sQuery(id+"F7.wireOp",EDGE,"E18"),sQuery(id+"F7.wireOp",EDGE,"E19"),sQuery(id+"F7.wireOp",EDGE,"E20"),sQuery(id+"F7.wireOp",EDGE,"E21"),sQuery(id+"F7.wireOp",EDGE,"E22"),sQuery(id+"F7.wireOp",EDGE,"E23"),sQuery(id+"F7.wireOp",EDGE,"E24"),sQuery(id+"F7.wireOp",EDGE,"E26"),sQuery(id+"F7.wireOp",EDGE,"E27"),sQuery(id+"F7.wireOp",EDGE,"E28"),sQuery(id+"F7.wireOp",EDGE,"E29"),sQuery(id+"F7.wireOp",EDGE,"E30"),sQuery(id+"F7.wireOp",EDGE,"E31"),sQuery(id+"F7.wireOp",EDGE,"E32"),sQuery(id+"F7.wireOp",EDGE,"E33"),sQuery(id+"F7.wireOp",EDGE,"E34"),sQuery(id+"F7.wireOp",EDGE,"E35"),sQuery(id+"F7.wireOp",EDGE,"E36"),sQuery(id+"F7.wireOp",EDGE,"E37.MirrorCS"),sQuery(id+"F7.wireOp",EDGE,"E38.MirrorCS"),sQuery(id+"F7.wireOp",EDGE,"E39.MirrorCS"),sQuery(id+"F7.wireOp",EDGE,"E40.MirrorCS"),sQuery(id+"F7.wireOp",EDGE,"E41.MirrorCS"),sQuery(id+"F7.wireOp",EDGE,"E42.MirrorCS"),sQuery(id+"F7.wireOp",EDGE,"E43.MirrorCS"),sQuery(id+"F7.wireOp",EDGE,"E44.MirrorCS"),sQuery(id+"F7.wireOp",EDGE,"E45.MirrorCS"),sQuery(id+"F7.wireOp",EDGE,"E46.MirrorCS"),sQuery(id+"F7.wireOp",EDGE,"E47.MirrorCS"),sQuery(id+"F7.wireOp",EDGE,"E48.MirrorCS"),sQuery(id+"F7.wireOp",EDGE,"E49.MirrorCS"),sQuery(id+"F7.wireOp",EDGE,"E50.MirrorCS")])],"isStart":false});
            var Q4;
            Q4=makeQuery(id+"F19.opExtrude","CAP_FACE",FACE,{"disambiguationData":[OSD([sQuery(id+"F17.wireOp",EDGE,"E125.bottom"),sQuery(id+"F17.wireOp",EDGE,"E125.top"),sQuery(id+"F17.wireOp",EDGE,"E125.left"),sQuery(id+"F17.wireOp",EDGE,"E125.right")])],"isStart":false});
            var Q5;
            Q5=makeQuery(id+"F19.opExtrude","CAP_FACE",FACE,{"disambiguationData":[OSD([sQuery(id+"F17.wireOp",EDGE,"E124.bottom"),sQuery(id+"F17.wireOp",EDGE,"E124.top"),sQuery(id+"F17.wireOp",EDGE,"E124.left"),sQuery(id+"F17.wireOp",EDGE,"E124.right")])],"isStart":false});
            var Q6;
            Q6=makeQuery(id+"F19.opExtrude","CAP_FACE",FACE,{"disambiguationData":[OSD([sQuery(id+"F17.wireOp",EDGE,"E123.bottom"),sQuery(id+"F17.wireOp",EDGE,"E123.top"),sQuery(id+"F17.wireOp",EDGE,"E123.left"),sQuery(id+"F17.wireOp",EDGE,"E123.right")])],"isStart":false});
            var Q7;
            Q7=makeQuery(id+"F19.opExtrude","CAP_FACE",FACE,{"disambiguationData":[OSD([sQuery(id+"F17.wireOp",EDGE,"E122.bottom"),sQuery(id+"F17.wireOp",EDGE,"E122.top"),sQuery(id+"F17.wireOp",EDGE,"E122.left"),sQuery(id+"F17.wireOp",EDGE,"E122.right")])],"isStart":false});
            var Q8;
            Q8=makeQuery(id+"F19.opExtrude","CAP_FACE",FACE,{"disambiguationData":[OSD([sQuery(id+"F17.wireOp",EDGE,"E121.bottom"),sQuery(id+"F17.wireOp",EDGE,"E121.top"),sQuery(id+"F17.wireOp",EDGE,"E121.left"),sQuery(id+"F17.wireOp",EDGE,"E121.right")])],"isStart":false});
            var Q9;
            Q9=makeQuery(id+"F19.opExtrude","CAP_FACE",FACE,{"disambiguationData":[OSD([sQuery(id+"F17.wireOp",EDGE,"E120.bottom"),sQuery(id+"F17.wireOp",EDGE,"E120.top"),sQuery(id+"F17.wireOp",EDGE,"E120.left"),sQuery(id+"F17.wireOp",EDGE,"E120.right")])],"isStart":false});
            var Q10;
            Q10=makeQuery(id+"F8.opExtrude","SWEPT_FACE",FACE,{"disambiguationData":[OSD([sQuery(id+"F7.wireOp",EDGE,"E17")])]});
            var Q11;
            Q11=makeQuery(id+"F12.boolean.opBoolean","MERGE",FACE,{"derivedFrom":[makeQuery(id+"F8.boolean.opBoolean","MERGE",FACE,{"derivedFrom":[makeQuery(id+"F2.opExtrude","SWEPT_FACE",FACE,{"disambiguationData":[OSD([sQuery(id+"F0.wireOp",EDGE,"E0.left")])]}),makeQuery(id+"F8.opExtrude","SWEPT_FACE",FACE,{"disambiguationData":[OSD([sQuery(id+"F7.wireOp",EDGE,"E19")])]})]}),makeQuery(id+"F12.opExtrude","SWEPT_FACE",FACE,{"disambiguationData":[OSD([sQuery(id+"F11.wireOp",EDGE,"E97")])]})]});
            var Q12;
            Q12=makeQuery(id+"F14.opExtrude","CAP_FACE",FACE,{"disambiguationData":[OSD([sQuery(id+"F13.wireOp",EDGE,"E98"),sQuery(id+"F13.wireOp",EDGE,"E99"),sQuery(id+"F13.wireOp",EDGE,"E100"),sQuery(id+"F13.wireOp",EDGE,"E101"),sQuery(id+"F13.wireOp",EDGE,"E102"),sQuery(id+"F13.wireOp",EDGE,"E103"),sQuery(id+"F13.wireOp",EDGE,"E104"),sQuery(id+"F13.wireOp",EDGE,"E105"),sQuery(id+"F13.wireOp",EDGE,"E106"),sQuery(id+"F13.wireOp",EDGE,"E107"),sQuery(id+"F13.wireOp",EDGE,"E108"),sQuery(id+"F13.wireOp",EDGE,"E109"),sQuery(id+"F13.wireOp",EDGE,"E110"),sQuery(id+"F13.wireOp",EDGE,"E111"),sQuery(id+"F13.wireOp",EDGE,"E112"),sQuery(id+"F13.wireOp",EDGE,"E113")])],"isStart":false});
            var Q13;
            Q13=makeQuery(id+"F10.opExtrude","CAP_FACE",FACE,{"disambiguationData":[OSD([sQuery(id+"F9.wireOp",EDGE,"E51"),sQuery(id+"F9.wireOp",EDGE,"E52"),sQuery(id+"F9.wireOp",EDGE,"E53"),sQuery(id+"F9.wireOp",EDGE,"E54"),sQuery(id+"F9.wireOp",EDGE,"E55"),sQuery(id+"F9.wireOp",EDGE,"E56"),sQuery(id+"F9.wireOp",EDGE,"E57"),sQuery(id+"F9.wireOp",EDGE,"E58"),sQuery(id+"F9.wireOp",EDGE,"E59"),sQuery(id+"F9.wireOp",EDGE,"E60"),sQuery(id+"F9.wireOp",EDGE,"E61"),sQuery(id+"F9.wireOp",EDGE,"E62"),sQuery(id+"F9.wireOp",EDGE,"E63"),sQuery(id+"F9.wireOp",EDGE,"E64"),sQuery(id+"F9.wireOp",EDGE,"E65"),sQuery(id+"F9.wireOp",EDGE,"E66"),sQuery(id+"F9.wireOp",EDGE,"E67"),sQuery(id+"F9.wireOp",EDGE,"E68"),sQuery(id+"F9.wireOp",EDGE,"E69"),sQuery(id+"F9.wireOp",EDGE,"E70"),sQuery(id+"F9.wireOp",EDGE,"E71"),sQuery(id+"F9.wireOp",EDGE,"E72"),sQuery(id+"F9.wireOp",EDGE,"E73.MirrorCS"),sQuery(id+"F9.wireOp",EDGE,"E74.MirrorCS"),sQuery(id+"F9.wireOp",EDGE,"E75.MirrorCS"),sQuery(id+"F9.wireOp",EDGE,"E76.MirrorCS"),sQuery(id+"F9.wireOp",EDGE,"E77.MirrorCS"),sQuery(id+"F9.wireOp",EDGE,"E78.MirrorCS"),sQuery(id+"F9.wireOp",EDGE,"E79.MirrorCS"),sQuery(id+"F9.wireOp",EDGE,"E80.MirrorCS"),sQuery(id+"F9.wireOp",EDGE,"E81"),sQuery(id+"F9.wireOp",EDGE,"E82")])],"isStart":false});
            var Q14;
            Q14=makeQuery(id+"F18.opExtrude","CAP_FACE",FACE,{"disambiguationData":[OSD([sQuery(id+"F16.wireOp",EDGE,"E114.bottom"),sQuery(id+"F16.wireOp",EDGE,"E114.top"),sQuery(id+"F16.wireOp",EDGE,"E114.left"),sQuery(id+"F16.wireOp",EDGE,"E114.right")])],"isStart":false});
            var Q15;
            Q15=makeQuery(id+"F18.opExtrude","CAP_FACE",FACE,{"disambiguationData":[OSD([sQuery(id+"F16.wireOp",EDGE,"E115.bottom"),sQuery(id+"F16.wireOp",EDGE,"E115.top"),sQuery(id+"F16.wireOp",EDGE,"E115.left"),sQuery(id+"F16.wireOp",EDGE,"E115.right")])],"isStart":false});
            var Q16;
            Q16=makeQuery(id+"F18.opExtrude","CAP_FACE",FACE,{"disambiguationData":[OSD([sQuery(id+"F16.wireOp",EDGE,"E116.bottom"),sQuery(id+"F16.wireOp",EDGE,"E116.top"),sQuery(id+"F16.wireOp",EDGE,"E116.left"),sQuery(id+"F16.wireOp",EDGE,"E116.right")])],"isStart":false});
            var Q17;
            Q17=makeQuery(id+"F18.opExtrude","CAP_FACE",FACE,{"disambiguationData":[OSD([sQuery(id+"F16.wireOp",EDGE,"E117.bottom"),sQuery(id+"F16.wireOp",EDGE,"E117.top"),sQuery(id+"F16.wireOp",EDGE,"E117.left"),sQuery(id+"F16.wireOp",EDGE,"E117.right")])],"isStart":false});
            var Q18;
            Q18=makeQuery(id+"F18.opExtrude","CAP_FACE",FACE,{"disambiguationData":[OSD([sQuery(id+"F16.wireOp",EDGE,"E118.bottom"),sQuery(id+"F16.wireOp",EDGE,"E118.top"),sQuery(id+"F16.wireOp",EDGE,"E118.left"),sQuery(id+"F16.wireOp",EDGE,"E118.right")])],"isStart":false});
            var Q19;
            Q19=makeQuery(id+"F18.opExtrude","SWEPT_FACE",FACE,{"disambiguationData":[OSD([sQuery(id+"F16.wireOp",EDGE,"E118.bottom")])]});
            var Q20;
            Q20=makeQuery(id+"F18.opExtrude","SWEPT_FACE",FACE,{"disambiguationData":[OSD([sQuery(id+"F16.wireOp",EDGE,"E117.bottom")])]});
            var Q21;
            Q21=makeQuery(id+"F18.opExtrude","SWEPT_FACE",FACE,{"disambiguationData":[OSD([sQuery(id+"F16.wireOp",EDGE,"E116.bottom")])]});
            var Q22;
            Q22=makeQuery(id+"F18.opExtrude","SWEPT_FACE",FACE,{"disambiguationData":[OSD([sQuery(id+"F16.wireOp",EDGE,"E115.bottom")])]});
            var Q23;
            Q23=makeQuery(id+"F18.opExtrude","SWEPT_FACE",FACE,{"disambiguationData":[OSD([sQuery(id+"F16.wireOp",EDGE,"E114.bottom")])]});
            var Q24;
            Q24=makeQuery(id+"F18.opExtrude","SWEPT_FACE",FACE,{"disambiguationData":[OSD([sQuery(id+"F16.wireOp",EDGE,"E114.top")])]});
            var Q25;
            Q25=makeQuery(id+"F18.opExtrude","SWEPT_FACE",FACE,{"disambiguationData":[OSD([sQuery(id+"F16.wireOp",EDGE,"E115.top")])]});
            var Q26;
            Q26=makeQuery(id+"F18.opExtrude","SWEPT_FACE",FACE,{"disambiguationData":[OSD([sQuery(id+"F16.wireOp",EDGE,"E116.top")])]});
            var Q27;
            Q27=makeQuery(id+"F18.opExtrude","SWEPT_FACE",FACE,{"disambiguationData":[OSD([sQuery(id+"F16.wireOp",EDGE,"E117.top")])]});
            var Q28;
            Q28=makeQuery(id+"F19.opExtrude","SWEPT_FACE",FACE,{"disambiguationData":[OSD([sQuery(id+"F17.wireOp",EDGE,"E125.top")])]});
            var Q29;
            Q29=makeQuery(id+"F19.opExtrude","SWEPT_FACE",FACE,{"disambiguationData":[OSD([sQuery(id+"F17.wireOp",EDGE,"E124.top")])]});
            var Q30;
            Q30=makeQuery(id+"F19.opExtrude","SWEPT_FACE",FACE,{"disambiguationData":[OSD([sQuery(id+"F17.wireOp",EDGE,"E122.top")])]});
            var Q31;
            Q31=makeQuery(id+"F19.opExtrude","SWEPT_FACE",FACE,{"disambiguationData":[OSD([sQuery(id+"F17.wireOp",EDGE,"E123.top")])]});
            var Q32;
            Q32=makeQuery(id+"F19.opExtrude","SWEPT_FACE",FACE,{"disambiguationData":[OSD([sQuery(id+"F17.wireOp",EDGE,"E121.top")])]});
            var Q33;
            Q33=makeQuery(id+"F19.opExtrude","SWEPT_FACE",FACE,{"disambiguationData":[OSD([sQuery(id+"F17.wireOp",EDGE,"E120.top")])]});
            var Q34;
            Q34=makeQuery(id+"F19.opExtrude","SWEPT_FACE",FACE,{"disambiguationData":[OSD([sQuery(id+"F17.wireOp",EDGE,"E120.bottom")])]});
            var Q35;
            Q35=makeQuery(id+"F19.opExtrude","SWEPT_FACE",FACE,{"disambiguationData":[OSD([sQuery(id+"F17.wireOp",EDGE,"E121.bottom")])]});
            var Q36;
            Q36=makeQuery(id+"F19.opExtrude","SWEPT_FACE",FACE,{"disambiguationData":[OSD([sQuery(id+"F17.wireOp",EDGE,"E122.bottom")])]});
            var Q37;
            Q37=makeQuery(id+"F19.opExtrude","SWEPT_FACE",FACE,{"disambiguationData":[OSD([sQuery(id+"F17.wireOp",EDGE,"E123.bottom")])]});
            var Q38;
            Q38=makeQuery(id+"F19.opExtrude","SWEPT_FACE",FACE,{"disambiguationData":[OSD([sQuery(id+"F17.wireOp",EDGE,"E124.bottom")])]});
            var Q39;
            Q39=makeQuery(id+"F19.opExtrude","SWEPT_FACE",FACE,{"disambiguationData":[OSD([sQuery(id+"F17.wireOp",EDGE,"E125.bottom")])]});
            var Q40;
            Q40=makeQuery(id+"F18.opExtrude","SWEPT_FACE",FACE,{"disambiguationData":[OSD([sQuery(id+"F16.wireOp",EDGE,"E118.top")])]});
            var Q41;
            Q41=makeQuery(id+"F10.opExtrude","SWEPT_FACE",FACE,{"disambiguationData":[OSD([sQuery(id+"F9.wireOp",EDGE,"E57")])]});
            var Q42;
            Q42=makeQuery(id+"F14.boolean.opBoolean","MERGE",FACE,{"derivedFrom":[makeQuery(id+"F10.boolean.opBoolean","MERGE",FACE,{"derivedFrom":[makeQuery(id+"F3.opPattern","COPY",FACE,{"derivedFrom":makeQuery(id+"F2.opExtrude","SWEPT_FACE",FACE,{"disambiguationData":[OSD([sQuery(id+"F0.wireOp",EDGE,"E0.left")])]}),"instanceName":"1"}),makeQuery(id+"F10.opExtrude","SWEPT_FACE",FACE,{"disambiguationData":[OSD([sQuery(id+"F9.wireOp",EDGE,"E55")])]})]}),makeQuery(id+"F14.opExtrude","SWEPT_FACE",FACE,{"disambiguationData":[OSD([sQuery(id+"F13.wireOp",EDGE,"E110")])]})]});
            var Q43;
            Q43=makeQuery(id+"F14.boolean.opBoolean","MERGE",FACE,{"derivedFrom":[makeQuery(id+"F3.opPattern","COPY",FACE,{"derivedFrom":makeQuery(id+"F2.opExtrude","SWEPT_FACE",FACE,{"disambiguationData":[OSD([sQuery(id+"F0.wireOp",EDGE,"E3")])]}),"instanceName":"1"}),makeQuery(id+"F14.opExtrude","SWEPT_FACE",FACE,{"disambiguationData":[OSD([sQuery(id+"F13.wireOp",EDGE,"E107")])]})]});
            var Q44;
            Q44=makeQuery(id+"F14.boolean.opBoolean","MERGE",FACE,{"derivedFrom":[makeQuery(id+"F3.opPattern","COPY",FACE,{"derivedFrom":makeQuery(id+"F2.opExtrude","SWEPT_FACE",FACE,{"disambiguationData":[OSD([sQuery(id+"F0.wireOp",EDGE,"E7")])]}),"instanceName":"1"}),makeQuery(id+"F14.opExtrude","SWEPT_FACE",FACE,{"disambiguationData":[OSD([sQuery(id+"F13.wireOp",EDGE,"E113")])]})]});
            var Q45;
            Q45=makeQuery(id+"F14.boolean.opBoolean","MERGE",FACE,{"derivedFrom":[makeQuery(id+"F3.opPattern","COPY",FACE,{"derivedFrom":makeQuery(id+"F2.opExtrude","SWEPT_FACE",FACE,{"disambiguationData":[OSD([sQuery(id+"F0.wireOp",EDGE,"E11")])]}),"instanceName":"1"}),makeQuery(id+"F14.opExtrude","SWEPT_FACE",FACE,{"disambiguationData":[OSD([sQuery(id+"F13.wireOp",EDGE,"E100")])]})]});
            var Q46;
            Q46=makeQuery(id+"F14.boolean.opBoolean","MERGE",FACE,{"derivedFrom":[makeQuery(id+"F3.opPattern","COPY",FACE,{"derivedFrom":makeQuery(id+"F2.opExtrude","SWEPT_FACE",FACE,{"disambiguationData":[OSD([sQuery(id+"F0.wireOp",EDGE,"E9")])]}),"instanceName":"1"}),makeQuery(id+"F14.opExtrude","SWEPT_FACE",FACE,{"disambiguationData":[OSD([sQuery(id+"F13.wireOp",EDGE,"E102")])]})]});
            var Q47;
            Q47=makeQuery(id+"F14.boolean.opBoolean","MERGE",FACE,{"derivedFrom":[makeQuery(id+"F3.opPattern","COPY",FACE,{"derivedFrom":makeQuery(id+"F2.opExtrude","SWEPT_FACE",FACE,{"disambiguationData":[OSD([sQuery(id+"F0.wireOp",EDGE,"E5")])]}),"instanceName":"1"}),makeQuery(id+"F14.opExtrude","SWEPT_FACE",FACE,{"disambiguationData":[OSD([sQuery(id+"F13.wireOp",EDGE,"E105")])]})]});
            var Q48;
            Q48=makeQuery(id+"F14.boolean.opBoolean","MERGE",FACE,{"derivedFrom":[makeQuery(id+"F3.opPattern","COPY",FACE,{"derivedFrom":makeQuery(id+"F2.opExtrude","SWEPT_FACE",FACE,{"disambiguationData":[OSD([sQuery(id+"F0.wireOp",EDGE,"E13")])]}),"instanceName":"1"}),makeQuery(id+"F14.opExtrude","SWEPT_FACE",FACE,{"disambiguationData":[OSD([sQuery(id+"F13.wireOp",EDGE,"E98")])]})]});
            var Q49;
            Q49=makeQuery(id+"F14.boolean.opBoolean","MERGE",FACE,{"derivedFrom":[makeQuery(id+"F3.opPattern","COPY",FACE,{"derivedFrom":makeQuery(id+"F2.opExtrude","SWEPT_FACE",FACE,{"disambiguationData":[OSD([sQuery(id+"F0.wireOp",EDGE,"E1")])]}),"instanceName":"1"}),makeQuery(id+"F14.opExtrude","SWEPT_FACE",FACE,{"disambiguationData":[OSD([sQuery(id+"F13.wireOp",EDGE,"E109")])]})]});
            var Q50;
            Q50=makeQuery(id+"F12.boolean.opBoolean","MERGE",FACE,{"derivedFrom":[makeQuery(id+"F2.opExtrude","SWEPT_FACE",FACE,{"disambiguationData":[OSD([sQuery(id+"F0.wireOp",EDGE,"E1")])]}),makeQuery(id+"F12.opExtrude","SWEPT_FACE",FACE,{"disambiguationData":[OSD([sQuery(id+"F11.wireOp",EDGE,"E83")])]})]});
            var Q51;
            Q51=makeQuery(id+"F12.boolean.opBoolean","MERGE",FACE,{"derivedFrom":[makeQuery(id+"F2.opExtrude","SWEPT_FACE",FACE,{"disambiguationData":[OSD([sQuery(id+"F0.wireOp",EDGE,"E3")])]}),makeQuery(id+"F12.opExtrude","SWEPT_FACE",FACE,{"disambiguationData":[OSD([sQuery(id+"F11.wireOp",EDGE,"E85")])]})]});
            var Q52;
            Q52=makeQuery(id+"F12.boolean.opBoolean","MERGE",FACE,{"derivedFrom":[makeQuery(id+"F2.opExtrude","SWEPT_FACE",FACE,{"disambiguationData":[OSD([sQuery(id+"F0.wireOp",EDGE,"E5")])]}),makeQuery(id+"F12.opExtrude","SWEPT_FACE",FACE,{"disambiguationData":[OSD([sQuery(id+"F11.wireOp",EDGE,"E87")])]})]});
            var Q53;
            {var subQ0=sQuery(id+"F0.wireOp",EDGE,"E7");Q53=makeQuery(id+"F12.boolean.opBoolean","MERGE",FACE,{"derivedFrom":[makeQuery(id+"F2.opExtrude","SWEPT_FACE",FACE,{"disambiguationData":[OSD([subQ0])]}),makeQuery(id+"F12.opExtrude","SWEPT_FACE",FACE,{"disambiguationData":[OSD([subQ0])]})]});}
            var Q54;
            Q54=makeQuery(id+"F12.boolean.opBoolean","MERGE",FACE,{"derivedFrom":[makeQuery(id+"F2.opExtrude","SWEPT_FACE",FACE,{"disambiguationData":[OSD([sQuery(id+"F0.wireOp",EDGE,"E9")])]}),makeQuery(id+"F12.opExtrude","SWEPT_FACE",FACE,{"disambiguationData":[OSD([sQuery(id+"F11.wireOp",EDGE,"E90")])]})]});
            var Q55;
            Q55=makeQuery(id+"F12.boolean.opBoolean","MERGE",FACE,{"derivedFrom":[makeQuery(id+"F2.opExtrude","SWEPT_FACE",FACE,{"disambiguationData":[OSD([sQuery(id+"F0.wireOp",EDGE,"E11")])]}),makeQuery(id+"F12.opExtrude","SWEPT_FACE",FACE,{"disambiguationData":[OSD([sQuery(id+"F11.wireOp",EDGE,"E92")])]})]});
            var Q56;
            Q56=makeQuery(id+"F12.boolean.opBoolean","MERGE",FACE,{"derivedFrom":[makeQuery(id+"F2.opExtrude","SWEPT_FACE",FACE,{"disambiguationData":[OSD([sQuery(id+"F0.wireOp",EDGE,"E13")])]}),makeQuery(id+"F12.opExtrude","SWEPT_FACE",FACE,{"disambiguationData":[OSD([sQuery(id+"F11.wireOp",EDGE,"E94")])]})]});
            var Q57;
            Q57=makeQuery(id+"F8.opExtrude","SWEPT_FACE",FACE,{"disambiguationData":[OSD([sQuery(id+"F7.wireOp",EDGE,"E22")])]});
            var Q58;
            {var subQ0=makeQuery(id+"F2.opExtrude","SWEPT_FACE",FACE,{"disambiguationData":[OSD([sQuery(id+"F1.wireOp",EDGE,"E14.bottom")])]});Q58=makeQuery(id+"F10.boolean.opBoolean","MERGE",FACE,{"derivedFrom":[makeQuery(id+"F8.boolean.opBoolean","MERGE",FACE,{"derivedFrom":[makeQuery(id+"F6.boolean.opBoolean","MERGE",FACE,{"derivedFrom":[subQ0,makeQuery(id+"F3.opPattern","COPY",FACE,{"derivedFrom":subQ0,"instanceName":"1"}),makeQuery(id+"F6.opExtrude","SWEPT_FACE",FACE,{"disambiguationData":[OSD([sQuery(id+"F5.wireOp",EDGE,"E16.top")])]})]}),makeQuery(id+"F8.opExtrude","SWEPT_FACE",FACE,{"disambiguationData":[OSD([sQuery(id+"F7.wireOp",EDGE,"E20")])]})]}),makeQuery(id+"F10.opExtrude","SWEPT_FACE",FACE,{"disambiguationData":[OSD([sQuery(id+"F9.wireOp",EDGE,"E54")])]})]});}
            var Q59;
            Q59=makeQuery(id+"F10.opExtrude","SWEPT_FACE",FACE,{"disambiguationData":[OSD([sQuery(id+"F9.wireOp",EDGE,"E52")])]});
            var Q60;
            Q60=makeQuery(id+"F10.opExtrude","SWEPT_FACE",FACE,{"disambiguationData":[OSD([sQuery(id+"F9.wireOp",EDGE,"E51")])]});
            var Q61;
            Q61=makeQuery(id+"F8.opExtrude","SWEPT_FACE",FACE,{"disambiguationData":[OSD([sQuery(id+"F7.wireOp",EDGE,"E23")])]});
            var Q62;
            Q62=makeQuery(id+"F18.opExtrude","SWEPT_FACE",FACE,{"disambiguationData":[OSD([sQuery(id+"F16.wireOp",EDGE,"E119.right")])]});
            var Q63;
            Q63=makeQuery(id+"F18.opExtrude","SWEPT_FACE",FACE,{"disambiguationData":[OSD([sQuery(id+"F16.wireOp",EDGE,"E119.left")])]});
            var Q64;
            Q64=makeQuery(id+"F18.opExtrude","CAP_FACE",FACE,{"disambiguationData":[OSD([sQuery(id+"F16.wireOp",EDGE,"E119.bottom"),sQuery(id+"F16.wireOp",EDGE,"E119.top"),sQuery(id+"F16.wireOp",EDGE,"E119.left"),sQuery(id+"F16.wireOp",EDGE,"E119.right")])],"isStart":false});
            fillet(context, id + "F20", {"entities" : qUnion([Q0, Q1, Q2, Q3, Q4, Q5, Q6, Q7, Q8, Q9, Q10, Q11, Q12, Q13, Q14, Q15, Q16, Q17, Q18, Q19, Q20, Q21, Q22, Q23, Q24, Q25, Q26, Q27, Q28, Q29, Q30, Q31, Q32, Q33, Q34, Q35, Q36, Q37, Q38, Q39, Q40, Q41, Q42, Q43, Q44, Q45, Q46, Q47, Q48, Q49, Q50, Q51, Q52, Q53, Q54, Q55, Q56, Q57, Q58, Q59, Q60, Q61, Q62, Q63, Q64]), "radius" : 0.3 * mm, "allowEdgeOverflow" : false});
        }
    });
